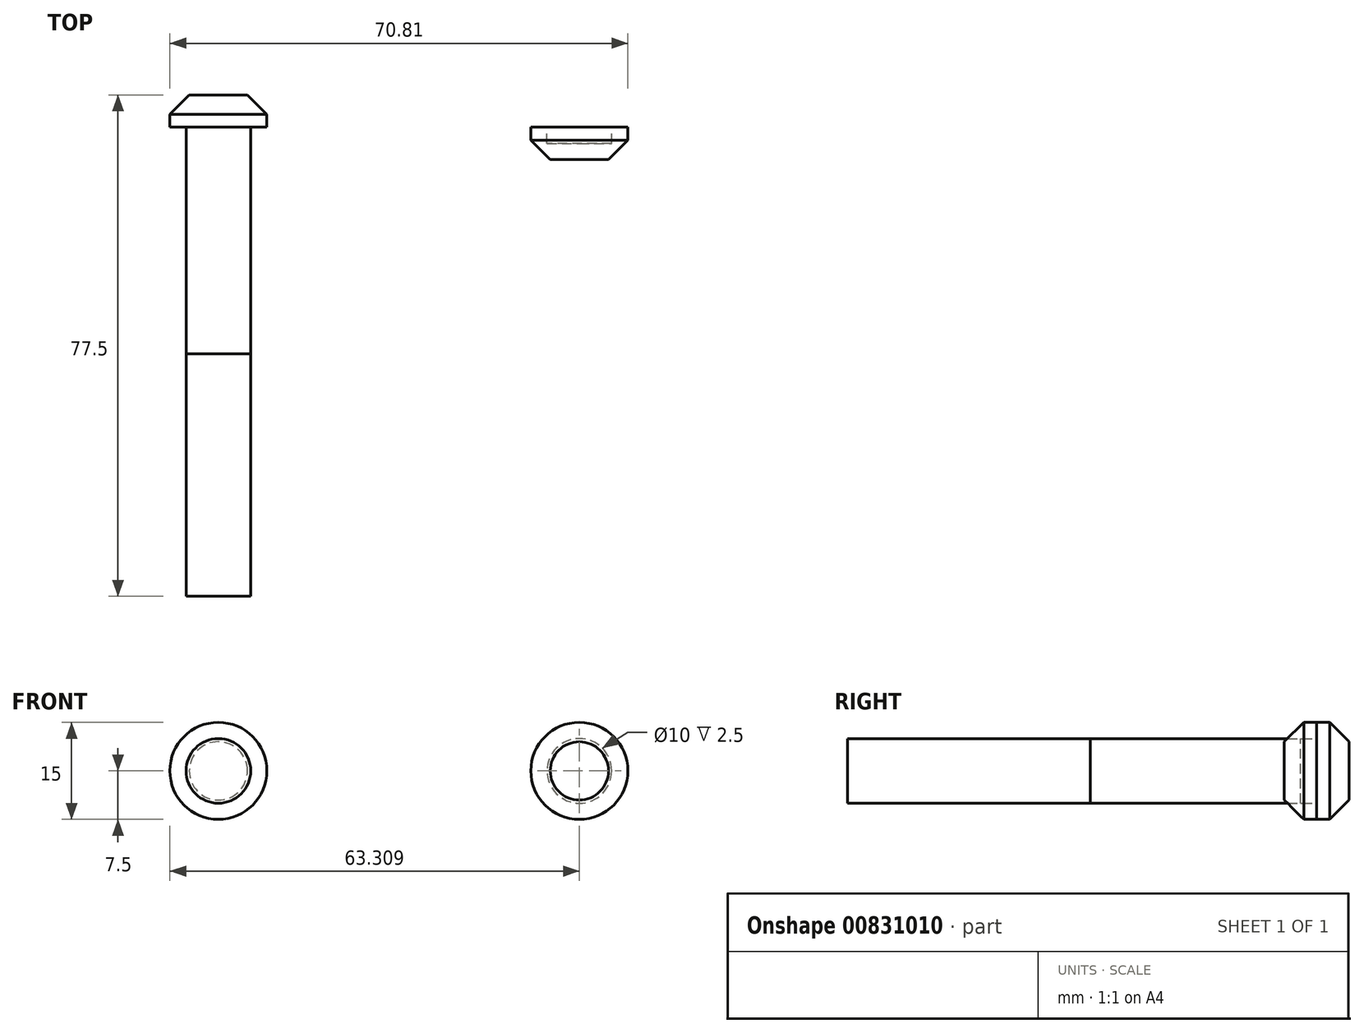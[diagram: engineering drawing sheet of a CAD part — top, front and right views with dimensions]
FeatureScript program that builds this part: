
annotation { "Feature Type Name" : "Feature", "Feature Type Description" : "" }
export const myFeature = defineFeature(function(context is Context, id is Id, definition is map)
    precondition{}
    {
        {
            var Q0;
            Q0=qCreatedBy(makeId("Front.planeOp"),FACE);
            var sketch = newSketch(context, id + "F0", { "sketchPlane" : qUnion([Q0])});
            skCircle(sketch, "E0", {"center": v(0, 0) * mm, "radius": 5 * mm});
            skCircle(sketch, "E1", {"center": v(0, 0) * mm, "radius": 7.5 * mm});
            skCircle(sketch, "E2", {"center": v(55.8, 0) * mm, "radius": 5 * mm});
            skCircle(sketch, "E3", {"center": v(55.8, 0) * mm, "radius": 7.5 * mm});
            skSolve(sketch);
        }
        {
            var Q0;
            Q0=makeQuery(id+"F0.imprint","IMPRINT",FACE,{"disambiguationData":[TD([[makeQuery(id+"F0.imprint","IMPRINT",EDGE,{"derivedFrom":sQuery(id+"F0.wireOp",EDGE,"E0")}),1.0]])]});
            extrude(context, id + "F1", {"entities" : qUnion([Q0]), "depth" : 35 * mm, "offsetDistance" : 25 * mm});
        }
        {
            var Q0;
            Q0=makeQuery(id+"F0.imprint","IMPRINT",FACE,{"disambiguationData":[TD([[makeQuery(id+"F0.imprint","IMPRINT",EDGE,{"derivedFrom":sQuery(id+"F0.wireOp",EDGE,"E0")}),-1.0]])]});
            var Q1;
            Q1=makeQuery(id+"F0.imprint","IMPRINT",FACE,{"disambiguationData":[TD([[makeQuery(id+"F0.imprint","IMPRINT",EDGE,{"derivedFrom":sQuery(id+"F0.wireOp",EDGE,"E0")}),1.0]])]});
            extrude(context, id + "F2", {"entities" : qUnion([Q0, Q1]), "operationType" : NewBodyOperationType.ADD, "oppositeDirection" : true, "depth" : 5 * mm, "offsetDistance" : 25 * mm});
        }
        {
            var Q0;
            Q0=makeQuery(id+"F0.imprint","IMPRINT",FACE,{"disambiguationData":[TD([[makeQuery(id+"F0.imprint","IMPRINT",EDGE,{"derivedFrom":sQuery(id+"F0.wireOp",EDGE,"E2")}),-1.0]])]});
            var Q1;
            Q1=makeQuery(id+"F0.imprint","IMPRINT",FACE,{"disambiguationData":[TD([[makeQuery(id+"F0.imprint","IMPRINT",EDGE,{"derivedFrom":sQuery(id+"F0.wireOp",EDGE,"E2")}),1.0]])]});
            extrude(context, id + "F3", {"entities" : qUnion([Q0, Q1]), "depth" : 5 * mm, "offsetDistance" : 25 * mm});
        }
        {
            var Q0;
            Q0=makeQuery(id+"F0.imprint","IMPRINT",FACE,{"disambiguationData":[TD([[makeQuery(id+"F0.imprint","IMPRINT",EDGE,{"derivedFrom":sQuery(id+"F0.wireOp",EDGE,"E2")}),1.0]])]});
            extrude(context, id + "F4", {"entities" : qUnion([Q0]), "operationType" : NewBodyOperationType.REMOVE, "depth" : 2.5 * mm, "offsetDistance" : 25 * mm});
        }
        {
            var Q0;
            Q0=makeQuery(id+"F1.opExtrude","CAP_FACE",FACE,{"disambiguationData":[OSD([sQuery(id+"F0.wireOp",EDGE,"E0")])],"isStart":false});
            var sketch = newSketch(context, id + "F5", { "sketchPlane" : qUnion([Q0])});
            skCircle(sketch, "E4", {"center": v(0, 0) * mm, "radius": 5 * mm});
            skSolve(sketch);
        }
        {
            var Q0;
            Q0=makeQuery(id+"F5.imprint","IMPRINT",FACE,{"disambiguationData":[TD([[makeQuery(id+"F5.imprint","IMPRINT",EDGE,{"derivedFrom":sQuery(id+"F5.wireOp",EDGE,"E4")}),1.0]])]});
            extrude(context, id + "F6", {"entities" : qUnion([Q0]), "depth" : 37.5 * mm, "offsetDistance" : 25 * mm});
        }
        {
            var Q0;
            Q0=makeQuery(id+"F2.opExtrude","CAP_EDGE",EDGE,{"disambiguationData":[OSD([sQuery(id+"F0.wireOp",EDGE,"E1")])],"isStart":false});
            chamfer(context, id + "F7", {"entities" : qUnion([Q0]), "width" : 3 * mm, "tangentPropagation" : true});
        }
        {
            var Q0;
            Q0=makeQuery(id+"F3.opExtrude","CAP_EDGE",EDGE,{"disambiguationData":[OSD([sQuery(id+"F0.wireOp",EDGE,"E3")])],"isStart":false});
            chamfer(context, id + "F8", {"entities" : qUnion([Q0]), "width" : 3 * mm, "tangentPropagation" : true});
        }
    });
